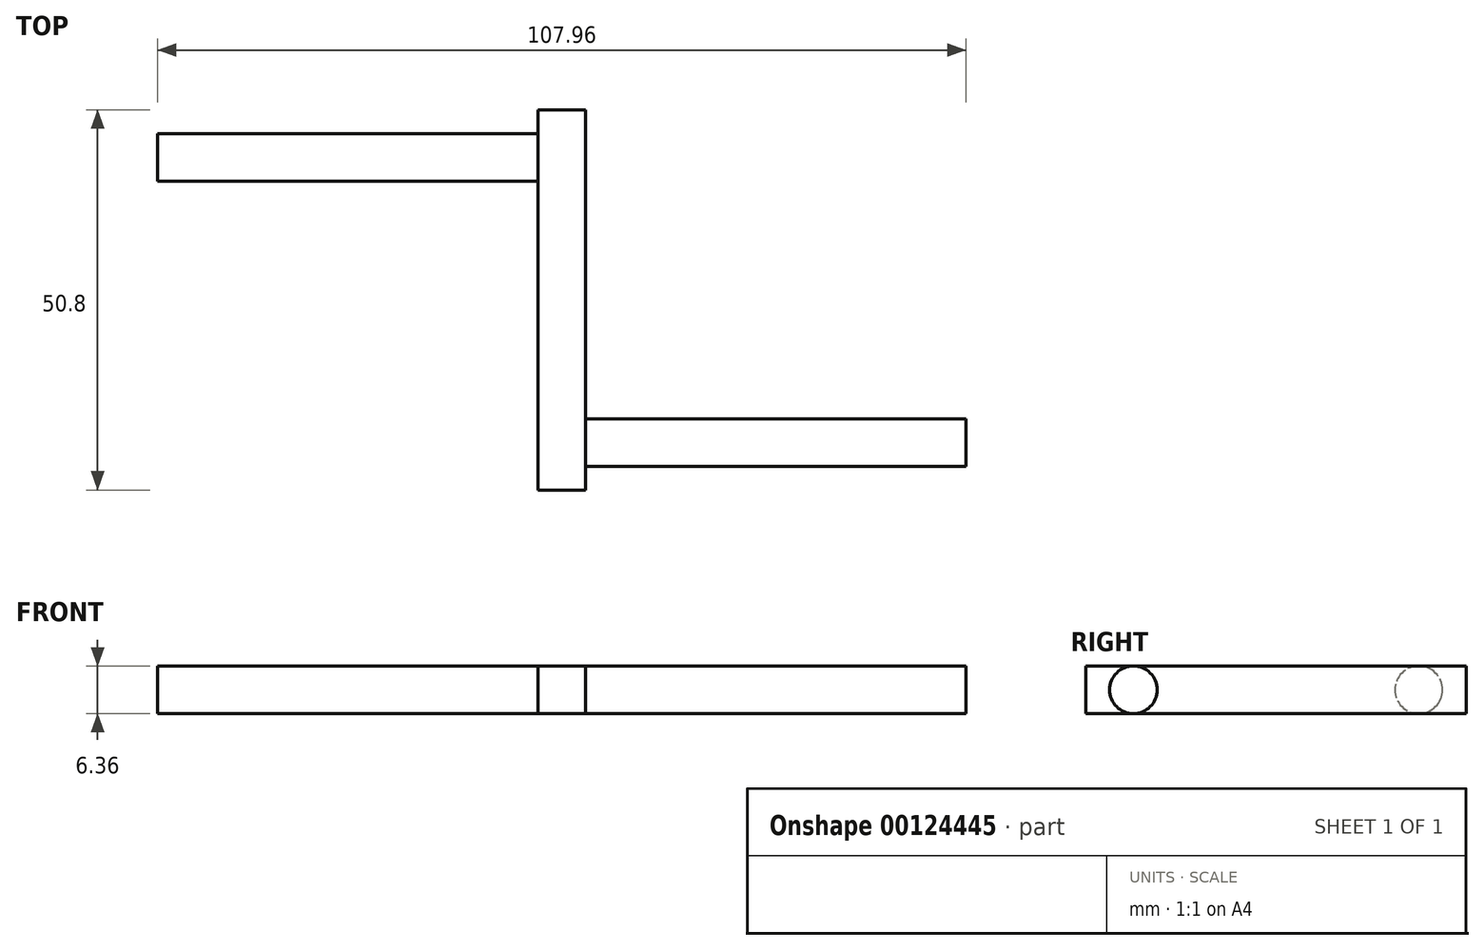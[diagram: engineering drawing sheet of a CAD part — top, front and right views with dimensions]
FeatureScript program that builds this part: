
annotation { "Feature Type Name" : "Feature", "Feature Type Description" : "" }
export const myFeature = defineFeature(function(context is Context, id is Id, definition is map)
    precondition{}
    {
        {
            var Q0;
            Q0=qCreatedBy(makeId("Front.planeOp"),FACE);
            var sketch = newSketch(context, id + "F0", { "sketchPlane" : qUnion([Q0])});
            skLineSegment(sketch, "E0.bottom", {"start": v(3.18, 3.18) * mm, "end": v(-3.17, 3.18) * mm});
            skLineSegment(sketch, "E0.top", {"start": v(3.17, -3.18) * mm, "end": v(-3.18, -3.18) * mm});
            skLineSegment(sketch, "E0.left", {"start": v(3.18, 3.18) * mm, "end": v(3.17, -3.18) * mm});
            skLineSegment(sketch, "E0.right", {"start": v(-3.17, 3.18) * mm, "end": v(-3.18, -3.18) * mm});
            skPoint(sketch, "E0.middle", {"position": v(0, 0) * mm});
            skSolve(sketch);
        }
        {
            var Q0;
            Q0 = qSketchRegion(id + "F0", true);
            extrude(context, id + "F1", {"entities" : qUnion([Q0]), "endBound" : BoundingType.SYMMETRIC, "depth" : 50.8 * mm});
        }
        {
            var Q0;
            Q0=makeQuery(id+"F1.opExtrude","SWEPT_FACE",FACE,{"disambiguationData":[OSD([sQuery(id+"F0.wireOp",EDGE,"E0.left")])]});
            var sketch = newSketch(context, id + "F2", { "sketchPlane" : qUnion([Q0])});
            skLineSegment(sketch, "E1", {"start": v(0, 0) * mm, "end": v(-19.05, 0) * mm});
            skCircle(sketch, "E2", {"center": v(-19.05, 0) * mm, "radius": 3.18 * mm});
            skSolve(sketch);
        }
        {
            var Q0;
            {var subQ0=sQuery(id+"F2.wireOp",EDGE,"E2");var subQ1=makeQuery(id+"F2.imprint","IMPRINT",VERTEX,{"derivedFrom":subQ0});Q0=makeQuery(id+"F2.imprint","IMPRINT",FACE,{"disambiguationData":[TD([[makeQuery(id+"F2.imprint","IMPRINT",EDGE,{"disambiguationData":[TD([[subQ1,-1.0]])],"derivedFrom":subQ0}),1.0]])]});}
            var Q1;
            Q1=sQuery(id+"F2.wireOp",EDGE,"E2");
            extrude(context, id + "F3", {"entities" : qUnion([Q0]), "operationType" : NewBodyOperationType.ADD, "surfaceEntities" : qUnion([Q1]), "depth" : 50.8 * mm});
        }
        {
            var Q0;
            Q0=makeQuery(id+"F1.opExtrude","SWEPT_FACE",FACE,{"disambiguationData":[OSD([sQuery(id+"F0.wireOp",EDGE,"E0.right")])]});
            var sketch = newSketch(context, id + "F4", { "sketchPlane" : qUnion([Q0])});
            skLineSegment(sketch, "E3", {"start": v(0, 0) * mm, "end": v(-19.05, 0) * mm});
            skCircle(sketch, "E4", {"center": v(-19.05, 0) * mm, "radius": 3.18 * mm});
            skSolve(sketch);
        }
        {
            var Q0;
            Q0 = qSketchRegion(id + "F4", true);
            extrude(context, id + "F5", {"entities" : qUnion([Q0]), "operationType" : NewBodyOperationType.ADD, "depth" : 50.8 * mm});
        }
    });
